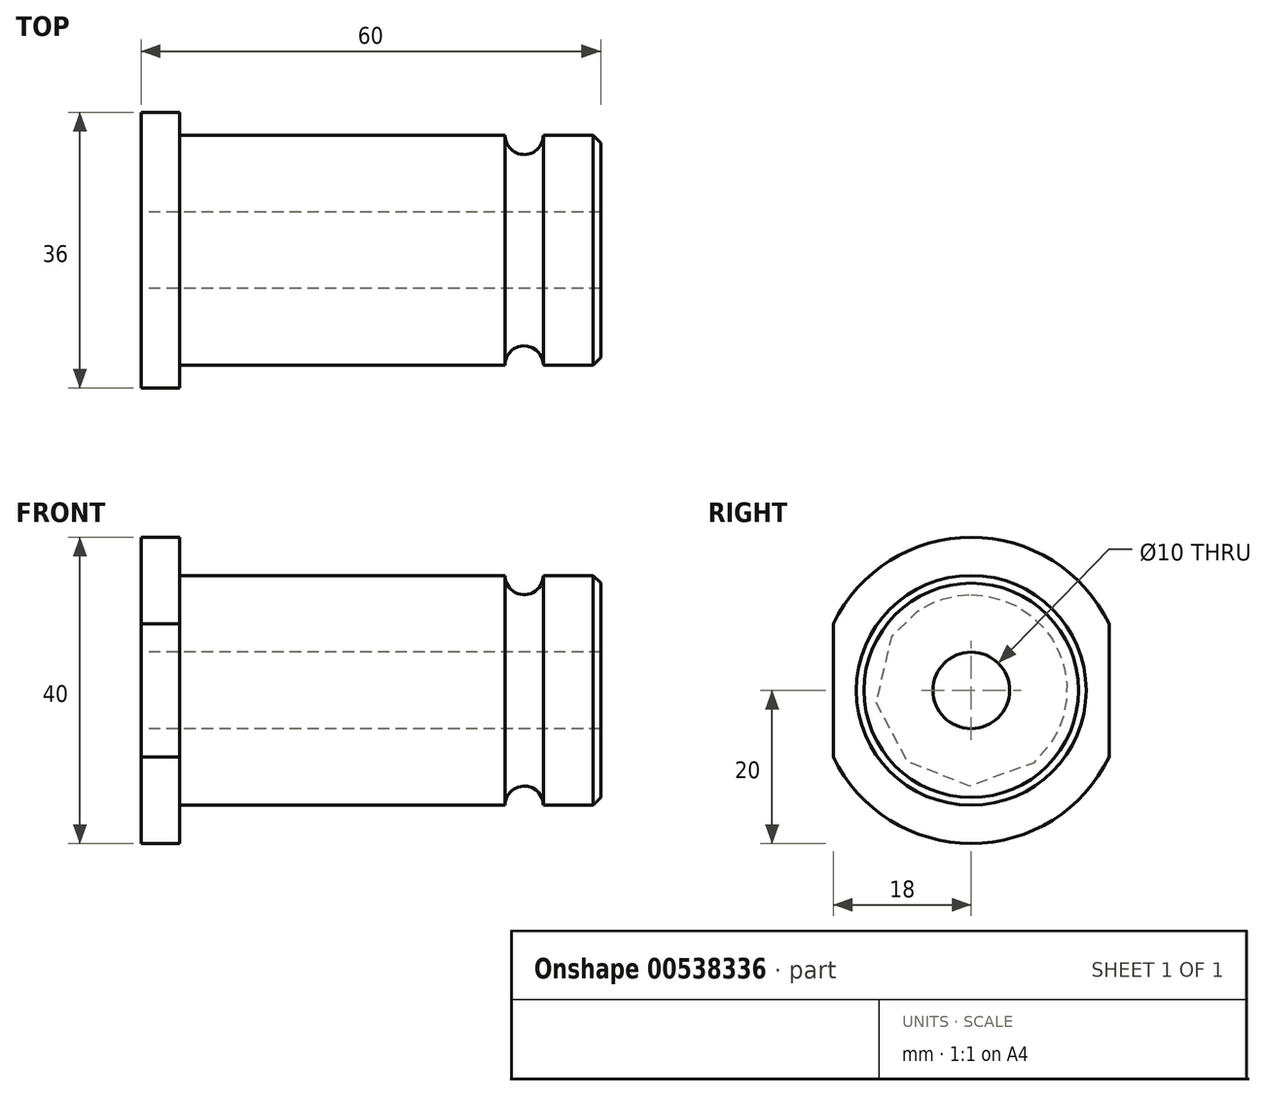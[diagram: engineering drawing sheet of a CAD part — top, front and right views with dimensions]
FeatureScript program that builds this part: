
annotation { "Feature Type Name" : "Feature", "Feature Type Description" : "" }
export const myFeature = defineFeature(function(context is Context, id is Id, definition is map)
    precondition{}
    {
        {
            var Q0;
            Q0=qCreatedBy(makeId("Front.planeOp"),FACE);
            var sketch = newSketch(context, id + "F0", { "sketchPlane" : qUnion([Q0])});
            skLineSegment(sketch, "E0", {"start": v(0, 0) * mm, "end": v(0, 20) * mm});
            skLineSegment(sketch, "E1", {"start": v(0, 20) * mm, "end": v(5, 20) * mm});
            skLineSegment(sketch, "E2", {"start": v(5, 20) * mm, "end": v(5, 15) * mm});
            skLineSegment(sketch, "E3", {"start": v(5, 15) * mm, "end": v(60, 15) * mm});
            skLineSegment(sketch, "E4", {"start": v(60, 15) * mm, "end": v(60, 0) * mm});
            skLineSegment(sketch, "E5", {"start": v(-12.34, 0) * mm, "end": v(76.6, 0) * mm, "construction": true});
            skLineSegment(sketch, "E6", {"start": v(0, 0) * mm, "end": v(60, 0) * mm});
            skSolve(sketch);
        }
        {
            var Q0;
            Q0=makeQuery(id+"F0.imprint","IMPRINT",FACE,{"disambiguationData":[TD([[makeQuery(id+"F0.imprint","IMPRINT",EDGE,{"derivedFrom":sQuery(id+"F0.wireOp",EDGE,"E0")}),-1.0]])]});
            var sketch = newSketch(context, id + "F1", { "sketchPlane" : qUnion([Q0])});
            skLineSegment(sketch, "E7", {"start": v(0, 0) * mm, "end": v(60, 0) * mm});
            skLineSegment(sketch, "E8", {"start": v(60, 0) * mm, "end": v(60, 15) * mm});
            skLineSegment(sketch, "E9", {"start": v(60, 15) * mm, "end": v(50, 15) * mm});
            skCircle(sketch, "E10", {"center": v(50, 15) * mm, "radius": 2.5 * mm});
            skSolve(sketch);
        }
        {
            var Q0;
            Q0=qSketchRegion(id+"F0",true);
            var Q1;
            Q1=sQuery(id+"F0.wireOp",EDGE,"E6");
            revolve(context, id + "F2", {"entities" : qUnion([Q0]), "axis" : qUnion([Q1]), "revolveType" : RevolveType.FULL});
        }
        {
            var Q0;
            Q0=makeQuery(id+"F2.opRevolve","SWEPT_EDGE",EDGE,{"disambiguationData":[OSD([sQuery(id+"F0.wireOp",EDGE,"E4"),sQuery(id+"F0.wireOp",EDGE,"DP23Sca5-nVmD-abGH-QyYi-Gxn6qPcy6v3g")])]});
            chamfer(context, id + "F3", {"entities" : qUnion([Q0]), "width" : 1 * mm, "tangentPropagation" : true});
        }
        {
            var Q0;
            Q0=qSketchRegion(id+"F1",true);
            var Q1;
            Q1=sQuery(id+"F1.wireOp",EDGE,"E7");
            revolve(context, id + "F4", {"operationType" : NewBodyOperationType.REMOVE, "entities" : qUnion([Q0]), "axis" : qUnion([Q1]), "revolveType" : RevolveType.FULL, "oppositeDirection" : true});
        }
        {
            var Q0;
            Q0=makeQuery(id+"F2.opRevolve","SWEPT_FACE",FACE,{"disambiguationData":[OSD([sQuery(id+"F0.wireOp",EDGE,"E0")])]});
            var sketch = newSketch(context, id + "F5", { "sketchPlane" : qUnion([Q0])});
            skLineSegment(sketch, "E11", {"start": v(0, -20) * mm, "end": v(-18, -20) * mm});
            skLineSegment(sketch, "E12.bottom", {"start": v(-18, -20) * mm, "end": v(18, -20) * mm});
            skLineSegment(sketch, "E12.top", {"start": v(-18, 20) * mm, "end": v(18, 20) * mm});
            skLineSegment(sketch, "E12.left", {"start": v(-18, -20) * mm, "end": v(-18, 20) * mm});
            skLineSegment(sketch, "E12.right", {"start": v(18, -20) * mm, "end": v(18, 20) * mm});
            skSolve(sketch);
        }
        {
            var Q0;
            {var subQ0=sQuery(id+"F5.wireOp",EDGE,"E12.right");var subQ1=makeQuery(id+"F2.opRevolve","SWEPT_EDGE",EDGE,{"disambiguationData":[OSD([sQuery(id+"F0.wireOp",EDGE,"E0"),sQuery(id+"F0.wireOp",EDGE,"E1")])]});var subQ2=makeQuery(id+"F5.imprint","INTERSECT",VERTEX,{"disambiguationData":[OD(0.0)],"derivedFrom":[subQ1,subQ0]});Q0=makeQuery(id+"F5.imprint","IMPRINT",FACE,{"disambiguationData":[TD([[makeQuery(id+"F5.imprint","IMPRINT",EDGE,{"disambiguationData":[TD([[subQ2,-1.0]])],"derivedFrom":subQ0}),-1.0]])]});}
            var Q1;
            {var subQ0=sQuery(id+"F5.wireOp",EDGE,"E12.left");var subQ1=makeQuery(id+"F2.opRevolve","SWEPT_EDGE",EDGE,{"disambiguationData":[OSD([sQuery(id+"F0.wireOp",EDGE,"E0"),sQuery(id+"F0.wireOp",EDGE,"E1")])]});var subQ2=makeQuery(id+"F5.imprint","INTERSECT",VERTEX,{"disambiguationData":[OD(0.0)],"derivedFrom":[subQ1,subQ0]});Q1=makeQuery(id+"F5.imprint","IMPRINT",FACE,{"disambiguationData":[TD([[makeQuery(id+"F5.imprint","IMPRINT",EDGE,{"disambiguationData":[TD([[subQ2,-1.0]])],"derivedFrom":subQ0}),1.0]])]});}
            extrude(context, id + "F6", {"entities" : qUnion([Q0, Q1]), "operationType" : NewBodyOperationType.REMOVE, "endBound" : BoundingType.UP_TO_NEXT, "oppositeDirection" : true, "depth" : 25 * mm, "offsetDistance" : 25 * mm});
        }
        {
            var Q0;
            Q0=makeQuery(id+"F2.opRevolve","SWEPT_FACE",FACE,{"disambiguationData":[OSD([sQuery(id+"F0.wireOp",EDGE,"E0")])]});
            var sketch = newSketch(context, id + "F7", { "sketchPlane" : qUnion([Q0])});
            skCircle(sketch, "E13", {"center": v(0, 0) * mm, "radius": 5 * mm});
            skSolve(sketch);
        }
        {
            var Q0;
            Q0=qSketchRegion(id+"F7",true);
            extrude(context, id + "F8", {"entities" : qUnion([Q0]), "operationType" : NewBodyOperationType.REMOVE, "endBound" : BoundingType.UP_TO_NEXT, "oppositeDirection" : true, "depth" : 25 * mm, "offsetDistance" : 25 * mm});
        }
    });
